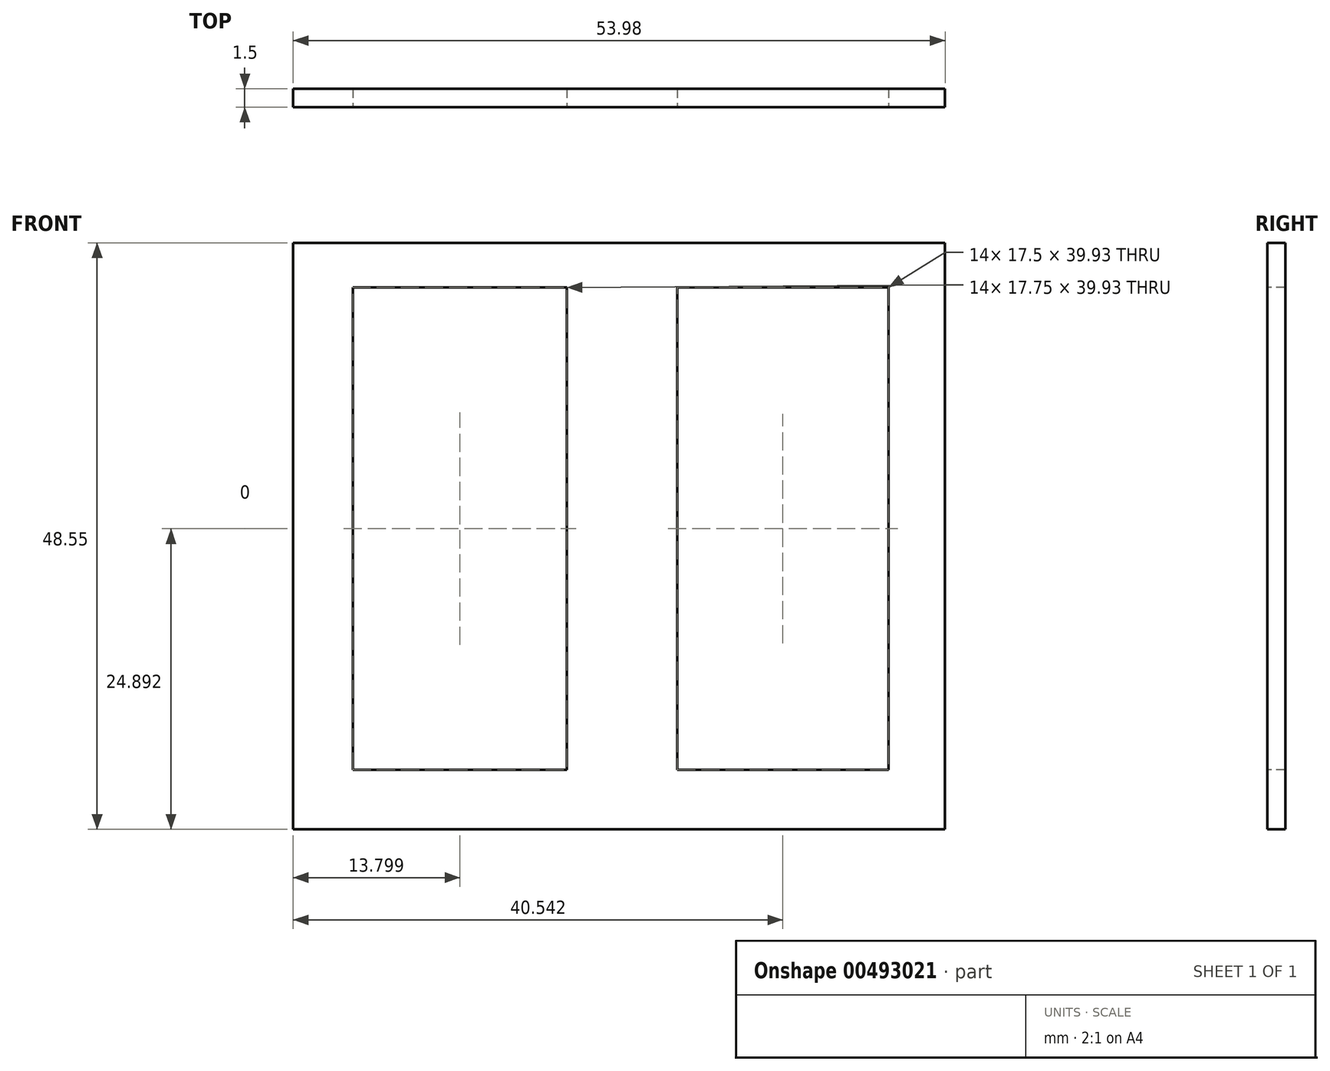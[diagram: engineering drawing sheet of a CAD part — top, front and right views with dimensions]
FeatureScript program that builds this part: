
annotation { "Feature Type Name" : "Feature", "Feature Type Description" : "" }
export const myFeature = defineFeature(function(context is Context, id is Id, definition is map)
    precondition{}
    {
        {
            var Q0;
            Q0=qCreatedBy(makeId("Front.planeOp"),FACE);
            var sketch = newSketch(context, id + "F0", { "sketchPlane" : qUnion([Q0])});
            skLineSegment(sketch, "E0.bottom", {"start": v(-39.31, -19.1) * mm, "end": v(14.67, -19.1) * mm});
            skLineSegment(sketch, "E0.top", {"start": v(-39.31, 29.45) * mm, "end": v(14.67, 29.45) * mm});
            skLineSegment(sketch, "E0.left", {"start": v(-39.31, -19.1) * mm, "end": v(-39.31, 29.45) * mm});
            skLineSegment(sketch, "E0.right", {"start": v(14.67, -19.1) * mm, "end": v(14.67, 29.45) * mm});
            skSolve(sketch);
        }
        {
            var Q0;
            Q0=makeQuery(id+"F0.imprint","IMPRINT",FACE,{"disambiguationData":[TD([[makeQuery(id+"F0.imprint","IMPRINT",EDGE,{"derivedFrom":sQuery(id+"F0.wireOp",EDGE,"E0.bottom")}),1.0]])]});
            extrude(context, id + "F1", {"entities" : qUnion([Q0]), "depth" : 1.5 * mm});
        }
        {
            var Q0;
            Q0=makeQuery(id+"F1.opExtrude","CAP_FACE",FACE,{"disambiguationData":[OSD([sQuery(id+"F0.wireOp",EDGE,"E0.bottom"),sQuery(id+"F0.wireOp",EDGE,"E0.top"),sQuery(id+"F0.wireOp",EDGE,"E0.left"),sQuery(id+"F0.wireOp",EDGE,"E0.right")])],"isStart":false});
            var sketch = newSketch(context, id + "F2", { "sketchPlane" : qUnion([Q0])});
            skLineSegment(sketch, "E1.bottom", {"start": v(-16.64, 25.76) * mm, "end": v(-34.38, 25.76) * mm});
            skLineSegment(sketch, "E1.top", {"start": v(-16.64, -14.17) * mm, "end": v(-34.38, -14.17) * mm});
            skLineSegment(sketch, "E1.left", {"start": v(-16.64, 25.76) * mm, "end": v(-16.64, -14.17) * mm});
            skLineSegment(sketch, "E1.right", {"start": v(-34.38, 25.76) * mm, "end": v(-34.38, -14.17) * mm});
            skLineSegment(sketch, "E2.bottom", {"start": v(9.98, -14.17) * mm, "end": v(-7.52, -14.17) * mm});
            skLineSegment(sketch, "E2.top", {"start": v(9.98, 25.76) * mm, "end": v(-7.52, 25.76) * mm});
            skLineSegment(sketch, "E2.left", {"start": v(9.98, -14.17) * mm, "end": v(9.98, 25.76) * mm});
            skLineSegment(sketch, "E2.right", {"start": v(-7.52, -14.17) * mm, "end": v(-7.52, 25.76) * mm});
            skSolve(sketch);
        }
        {
            var Q0;
            Q0 = qSketchRegion(id + "F2", true);
            extrude(context, id + "F3", {"entities" : qUnion([Q0]), "operationType" : NewBodyOperationType.REMOVE, "oppositeDirection" : true, "depth" : 1.5 * mm});
        }
    });
